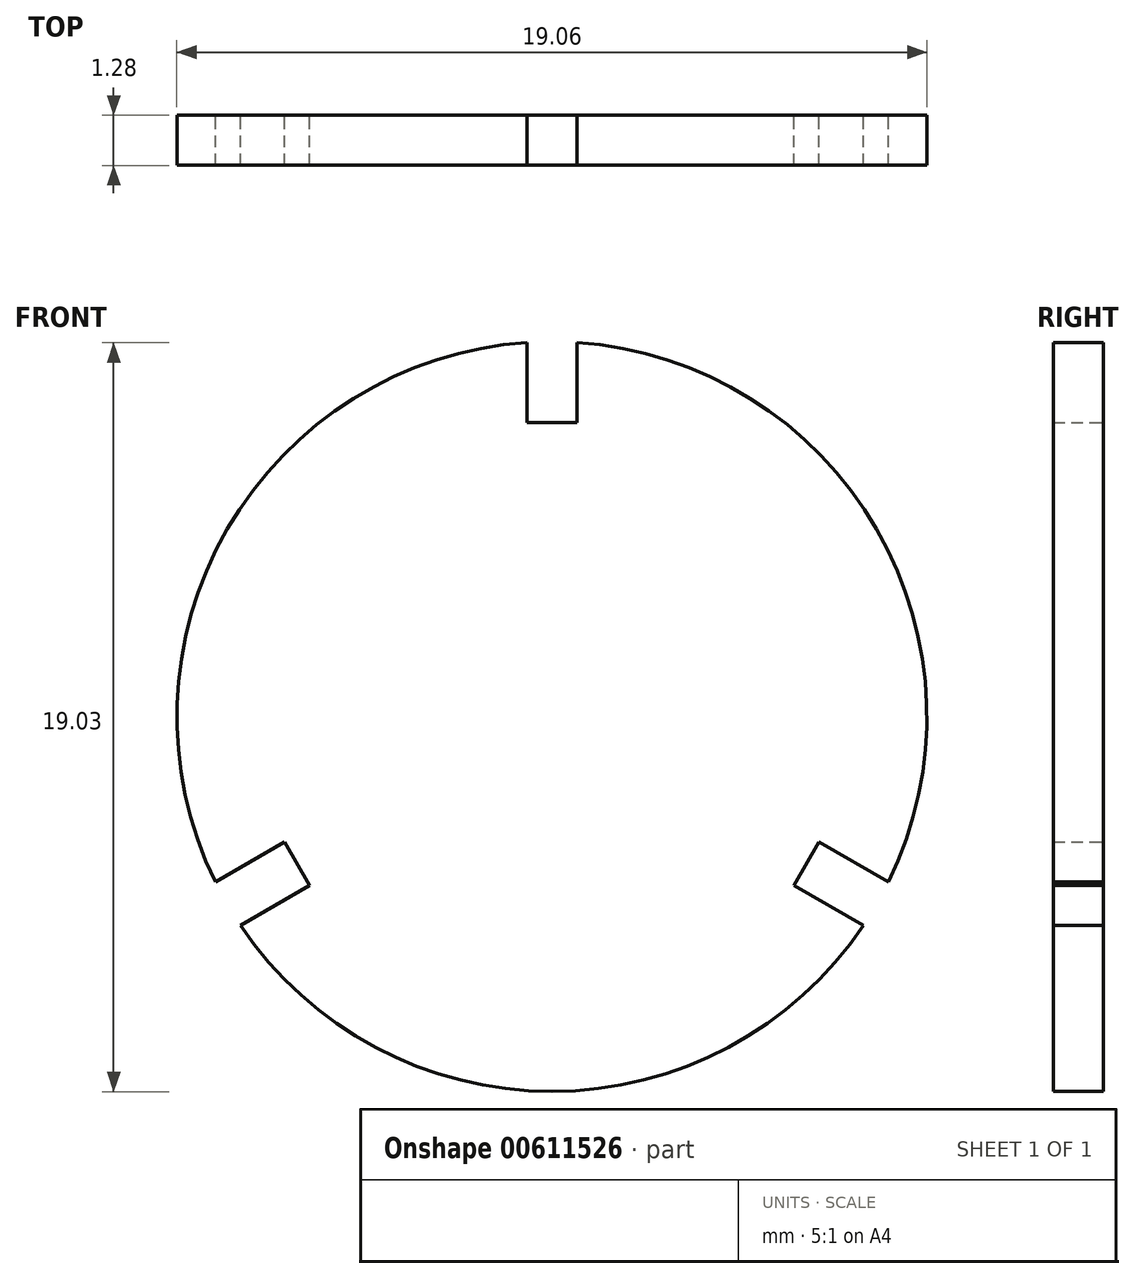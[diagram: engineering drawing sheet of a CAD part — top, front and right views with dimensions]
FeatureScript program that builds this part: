
annotation { "Feature Type Name" : "Feature", "Feature Type Description" : "" }
export const myFeature = defineFeature(function(context is Context, id is Id, definition is map)
    precondition{}
    {
        {
            var Q0;
            Q0=qCreatedBy(makeId("Front.planeOp"),FACE);
            var sketch = newSketch(context, id + "F0", { "sketchPlane" : qUnion([Q0])});
            skArc(sketch, "E0", {"start": v(-0.64, 9.5) * mm, "mid": v(-8.25, 4.76) * mm, "end": v(-8.55, -4.2) * mm});
            skLineSegment(sketch, "E1.top", {"start": v(-0.64, 7.47) * mm, "end": v(0.64, 7.47) * mm});
            skLineSegment(sketch, "E1.left", {"start": v(-0.64, 9.5) * mm, "end": v(-0.64, 7.47) * mm});
            skLineSegment(sketch, "E1.right", {"start": v(0.64, 9.5) * mm, "end": v(0.64, 7.47) * mm});
            skLineSegment(sketch, "E2.1.0", {"start": v(-8.55, -4.2) * mm, "end": v(-6.79, -3.19) * mm});
            skLineSegment(sketch, "E2.1.1", {"start": v(-6.15, -4.29) * mm, "end": v(-6.79, -3.19) * mm});
            skLineSegment(sketch, "E2.1.2", {"start": v(-7.91, -5.3) * mm, "end": v(-6.15, -4.29) * mm});
            skLineSegment(sketch, "E2.2.0", {"start": v(7.91, -5.3) * mm, "end": v(6.15, -4.29) * mm});
            skLineSegment(sketch, "E2.2.1", {"start": v(6.79, -3.19) * mm, "end": v(6.15, -4.29) * mm});
            skLineSegment(sketch, "E2.2.2", {"start": v(8.55, -4.2) * mm, "end": v(6.79, -3.19) * mm});
            skArc(sketch, "E3.trimOffspring", {"start": v(8.55, -4.2) * mm, "mid": v(8.25, 4.76) * mm, "end": v(0.64, 9.5) * mm});
            skArc(sketch, "E4.trimOffspring", {"start": v(-7.91, -5.3) * mm, "mid": v(0, -9.53) * mm, "end": v(7.91, -5.3) * mm});
            skSolve(sketch);
        }
        {
            var Q0;
            Q0=makeQuery(id+"F0.imprint","IMPRINT",FACE,{"disambiguationData":[TD([[makeQuery(id+"F0.imprint","IMPRINT",EDGE,{"derivedFrom":sQuery(id+"F0.wireOp",EDGE,"E0")}),1.0]])]});
            extrude(context, id + "F1", {"entities" : qUnion([Q0]), "endBound" : BoundingType.SYMMETRIC, "depth" : 1.27 * mm, "offsetDistance" : 25.4 * mm});
        }
    });
